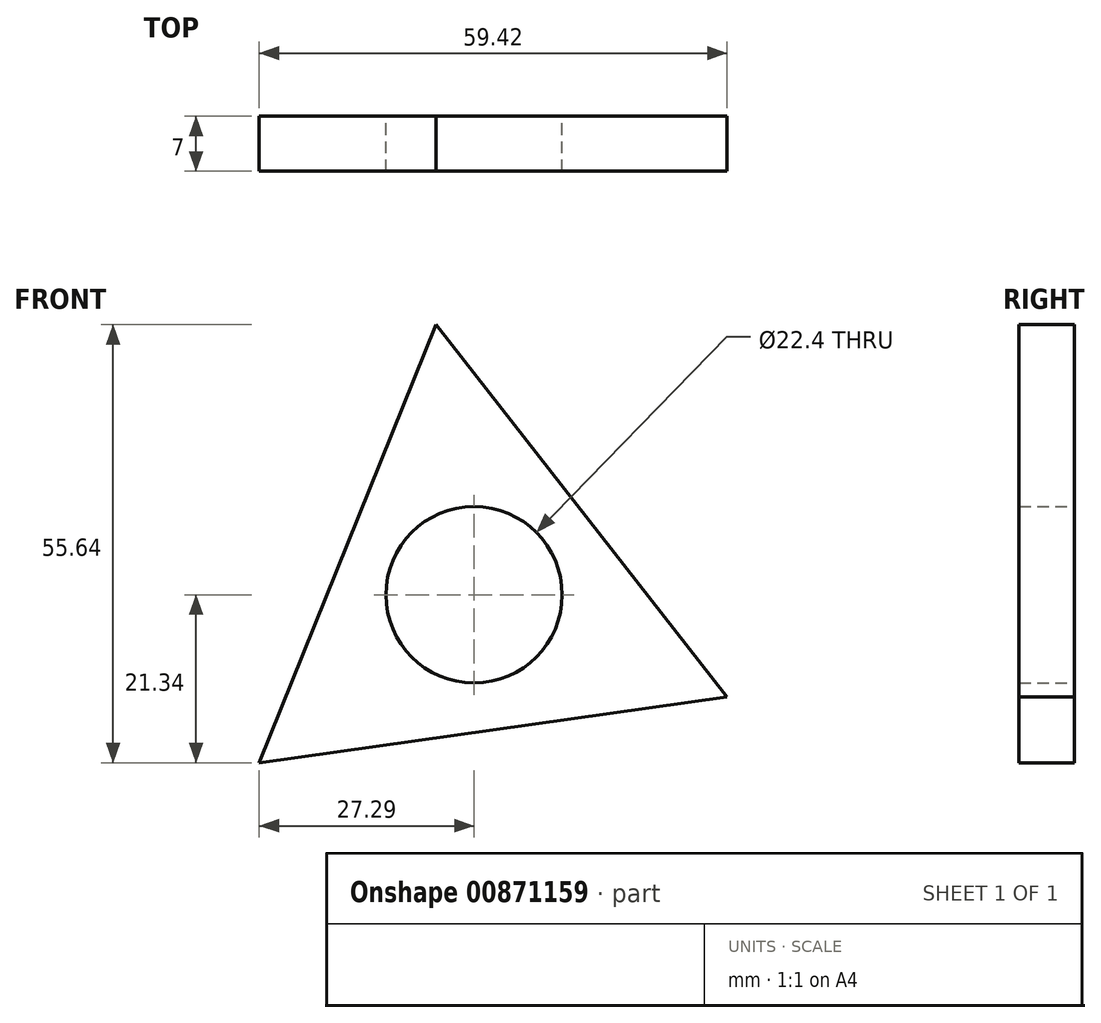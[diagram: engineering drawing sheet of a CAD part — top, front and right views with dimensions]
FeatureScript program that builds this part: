
annotation { "Feature Type Name" : "Feature", "Feature Type Description" : "" }
export const myFeature = defineFeature(function(context is Context, id is Id, definition is map)
    precondition{}
    {
        {
            var Q0;
            Q0=qCreatedBy(makeId("Front.planeOp"),FACE);
            var sketch = newSketch(context, id + "F0", { "sketchPlane" : qUnion([Q0])});
            skCircle(sketch, "E0", {"center": v(0, 0) * mm, "radius": 11.2 * mm});
            skCircle(sketch, "E1.cCircle", {"center": v(0, 0) * mm, "radius": 17.32 * mm, "construction": true});
            skLineSegment(sketch, "E1.0", {"start": v(-4.84, 34.3) * mm, "end": v(32.13, -12.96) * mm});
            skLineSegment(sketch, "E1.1", {"start": v(32.13, -12.96) * mm, "end": v(-27.29, -21.34) * mm});
            skLineSegment(sketch, "E1.2", {"start": v(-27.29, -21.34) * mm, "end": v(-4.84, 34.3) * mm});
            skPoint(sketch, "E1.0.midPoint", {"position": v(13.64, 10.67) * mm});
            skSolve(sketch);
        }
        {
            var Q0;
            Q0=makeQuery(id+"F0.imprint","IMPRINT",FACE,{"disambiguationData":[TD([[makeQuery(id+"F0.imprint","IMPRINT",EDGE,{"derivedFrom":sQuery(id+"F0.wireOp",EDGE,"E0")}),-1.0]])]});
            extrude(context, id + "F1", {"entities" : qUnion([Q0]), "depth" : 7 * mm, "offsetDistance" : 25 * mm});
        }
    });
